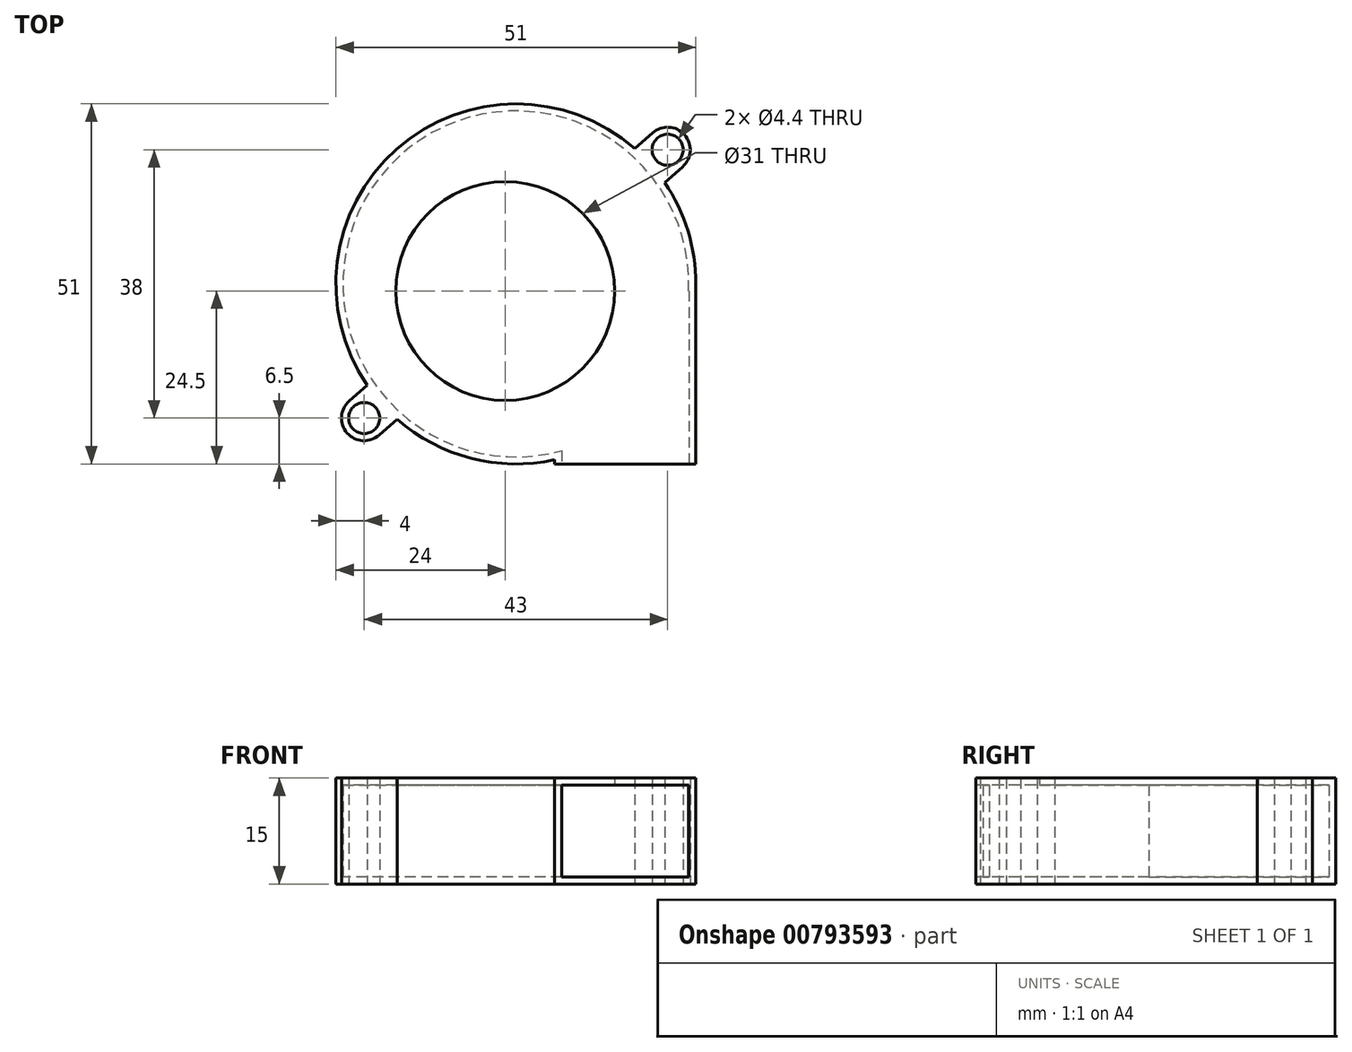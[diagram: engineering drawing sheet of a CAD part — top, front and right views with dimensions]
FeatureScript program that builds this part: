
annotation { "Feature Type Name" : "Feature", "Feature Type Description" : "" }
export const myFeature = defineFeature(function(context is Context, id is Id, definition is map)
    precondition{}
    {
        {
            assignVariable(context, id + "F0", {"name" : "thickness", "anyValue" : 15});
        }
        {
            var Q0;
            Q0=qCreatedBy(makeId("Top.planeOp"),FACE);
            var sketch = newSketch(context, id + "F1", { "sketchPlane" : qUnion([Q0])});
            skLineSegment(sketch, "E0.bottom", {"start": v(25.5, -25.5) * mm, "end": v(-25.5, -25.5) * mm});
            skLineSegment(sketch, "E0.top", {"start": v(25.5, 25.5) * mm, "end": v(-25.5, 25.5) * mm});
            skLineSegment(sketch, "E0.left", {"start": v(25.5, -25.5) * mm, "end": v(25.5, 25.5) * mm});
            skLineSegment(sketch, "E0.right", {"start": v(-25.5, -25.5) * mm, "end": v(-25.5, 25.5) * mm});
            skPoint(sketch, "E0.middle", {"position": v(0, 0) * mm});
            skLineSegment(sketch, "E1.bottom", {"start": v(21.5, -19) * mm, "end": v(-21.5, -19) * mm, "construction": true});
            skLineSegment(sketch, "E1.top", {"start": v(21.5, 19) * mm, "end": v(-21.5, 19) * mm, "construction": true});
            skLineSegment(sketch, "E1.left", {"start": v(21.5, -19) * mm, "end": v(21.5, 19) * mm, "construction": true});
            skLineSegment(sketch, "E1.right", {"start": v(-21.5, -19) * mm, "end": v(-21.5, 19) * mm, "construction": true});
            skCircle(sketch, "E2", {"center": v(0, 0) * mm, "radius": 25.5 * mm});
            skCircle(sketch, "E3", {"center": v(-21.5, -19) * mm, "radius": 2.2 * mm});
            skCircle(sketch, "E4", {"center": v(21.5, 19) * mm, "radius": 2.2 * mm});
            skCircle(sketch, "E5", {"center": v(-21.5, -19) * mm, "radius": 3.2 * mm});
            skCircle(sketch, "E6", {"center": v(21.5, 19) * mm, "radius": 3.2 * mm});
            skLineSegment(sketch, "E7", {"start": v(-21.5, -19) * mm, "end": v(0, 0) * mm, "construction": true});
            skLineSegment(sketch, "E8", {"start": v(21.5, 19) * mm, "end": v(0, 0) * mm, "construction": true});
            skLineSegment(sketch, "E9", {"start": v(-23.62, -16.6) * mm, "end": v(-21.08, -14.35) * mm});
            skLineSegment(sketch, "E10", {"start": v(-19.38, -21.4) * mm, "end": v(-16.84, -19.15) * mm});
            skLineSegment(sketch, "E11", {"start": v(19.38, 21.4) * mm, "end": v(16.84, 19.15) * mm});
            skLineSegment(sketch, "E12", {"start": v(23.62, 16.6) * mm, "end": v(21.08, 14.35) * mm});
            skLineSegment(sketch, "E13", {"start": v(5.5, -25.5) * mm, "end": v(5.5, -24.9) * mm});
            skCircle(sketch, "E14", {"center": v(-1.5, -1) * mm, "radius": 15.5 * mm});
            skCircle(sketch, "E15", {"center": v(0, 0) * mm, "radius": 24.5 * mm});
            skSolve(sketch);
        }
        {
            var Q0;
            {var subQ3=sQuery(id+"F1.wireOp",EDGE,"E13");Q0=makeQuery(id+"F1.imprint","IMPRINT",FACE,{"disambiguationData":[TD([[makeQuery(id+"F1.imprint","IMPRINT",EDGE,{"derivedFrom":subQ3}),-1.0]])]});}
            var Q1;
            Q1=makeQuery(id+"F1.imprint","IMPRINT",FACE,{"disambiguationData":[TD([[makeQuery(id+"F1.imprint","IMPRINT",EDGE,{"derivedFrom":sQuery(id+"F1.wireOp",EDGE,"E14")}),-1.0]])]});
            var Q2;
            {var subQ0=sQuery(id+"F1.wireOp",EDGE,"E10");Q2=makeQuery(id+"F1.imprint","IMPRINT",FACE,{"disambiguationData":[TD([[makeQuery(id+"F1.imprint","IMPRINT",EDGE,{"derivedFrom":subQ0}),1.0]])]});}
            var Q3;
            Q3=makeQuery(id+"F1.imprint","IMPRINT",FACE,{"disambiguationData":[TD([[makeQuery(id+"F1.imprint","IMPRINT",EDGE,{"derivedFrom":sQuery(id+"F1.wireOp",EDGE,"E3")}),-1.0]])]});
            var Q4;
            {var subQ0=sQuery(id+"F1.wireOp",EDGE,"E9");Q4=makeQuery(id+"F1.imprint","IMPRINT",FACE,{"disambiguationData":[TD([[makeQuery(id+"F1.imprint","IMPRINT",EDGE,{"derivedFrom":subQ0}),-1.0]])]});}
            var Q5;
            {var subQ0=sQuery(id+"F1.wireOp",EDGE,"E12");Q5=makeQuery(id+"F1.imprint","IMPRINT",FACE,{"disambiguationData":[TD([[makeQuery(id+"F1.imprint","IMPRINT",EDGE,{"derivedFrom":subQ0}),-1.0]])]});}
            var Q6;
            {var subQ0=sQuery(id+"F1.wireOp",EDGE,"E11");Q6=makeQuery(id+"F1.imprint","IMPRINT",FACE,{"disambiguationData":[TD([[makeQuery(id+"F1.imprint","IMPRINT",EDGE,{"derivedFrom":subQ0}),1.0]])]});}
            var Q7;
            Q7=makeQuery(id+"F1.imprint","IMPRINT",FACE,{"disambiguationData":[TD([[makeQuery(id+"F1.imprint","IMPRINT",EDGE,{"derivedFrom":sQuery(id+"F1.wireOp",EDGE,"E4")}),-1.0]])]});
            var Q8;
            Q8=makeQuery(id+"F1.imprint","IMPRINT",FACE,{"disambiguationData":[TD([[makeQuery(id+"F1.imprint","IMPRINT",EDGE,{"derivedFrom":sQuery(id+"F1.wireOp",EDGE,"E14")}),1.0]])]});
            var Q9;
            Q9=makeQuery(id+"F1.imprint","IMPRINT",FACE,{"disambiguationData":[TD([[makeQuery(id+"F1.imprint","IMPRINT",EDGE,{"derivedFrom":sQuery(id+"F1.wireOp",EDGE,"E15")}),-1.0]])]});
            var Q10;
            {var subQ0=sQuery(id+"F1.wireOp",EDGE,"E5");var subQ1=sQuery(id+"F1.wireOp",EDGE,"E2");var subQ2=makeQuery(id+"F1.imprint","INTERSECT",VERTEX,{"disambiguationData":[OD(0.0)],"derivedFrom":[subQ1,subQ0]});Q10=makeQuery(id+"F1.imprint","IMPRINT",FACE,{"disambiguationData":[TD([[makeQuery(id+"F1.imprint","IMPRINT",EDGE,{"disambiguationData":[TD([[subQ2,-1.0]])],"derivedFrom":subQ1}),1.0]])]});}
            var Q11;
            {var subQ0=sQuery(id+"F1.wireOp",EDGE,"E6");var subQ1=sQuery(id+"F1.wireOp",EDGE,"E2");var subQ2=makeQuery(id+"F1.imprint","INTERSECT",VERTEX,{"disambiguationData":[OD(0.0)],"derivedFrom":[subQ1,subQ0]});Q11=makeQuery(id+"F1.imprint","IMPRINT",FACE,{"disambiguationData":[TD([[makeQuery(id+"F1.imprint","IMPRINT",EDGE,{"disambiguationData":[TD([[subQ2,-1.0]])],"derivedFrom":subQ1}),1.0]])]});}
            extrude(context, id + "F2", {"entities" : qUnion([Q0, Q1, Q2, Q3, Q4, Q5, Q6, Q7, Q8, Q9, Q10, Q11]), "depth" : (getVariable(context, 'thickness')) * mm, "offsetDistance" : 25 * mm});
        }
        {
            var Q0;
            Q0=makeQuery(id+"F1.imprint","IMPRINT",FACE,{"disambiguationData":[TD([[makeQuery(id+"F1.imprint","IMPRINT",EDGE,{"derivedFrom":sQuery(id+"F1.wireOp",EDGE,"E14")}),1.0]])]});
            extrude(context, id + "F3", {"entities" : qUnion([Q0]), "operationType" : NewBodyOperationType.REMOVE, "depth" : 25 * mm, "offsetDistance" : 25 * mm, "hasSecondDirection" : true, "secondDirectionOppositeDirection" : false, "secondDirectionDepth" : 1 * mm});
        }
        {
            var Q0;
            Q0=makeQuery(id+"F1.imprint","IMPRINT",FACE,{"disambiguationData":[TD([[makeQuery(id+"F1.imprint","IMPRINT",EDGE,{"derivedFrom":sQuery(id+"F1.wireOp",EDGE,"E14")}),-1.0]])]});
            var Q1;
            Q1=makeQuery(id+"F1.imprint","IMPRINT",FACE,{"disambiguationData":[TD([[makeQuery(id+"F1.imprint","IMPRINT",EDGE,{"derivedFrom":sQuery(id+"F1.wireOp",EDGE,"E14")}),1.0]])]});
            extrude(context, id + "F4", {"entities" : qUnion([Q0, Q1]), "operationType" : NewBodyOperationType.REMOVE, "depth" : (getVariable(context, 'thickness') - 1) * mm, "offsetDistance" : 25 * mm, "hasSecondDirection" : true, "secondDirectionOppositeDirection" : false, "secondDirectionDepth" : 1 * mm});
        }
        {
            var Q0;
            Q0=makeQuery(id+"F2.opExtrude","SWEPT_FACE",FACE,{"disambiguationData":[OSD([sQuery(id+"F1.wireOp",EDGE,"E0.bottom")])]});
            var sketch = newSketch(context, id + "F5", { "sketchPlane" : qUnion([Q0])});
            skLineSegment(sketch, "E16.bottom", {"start": v(24.5, 1) * mm, "end": v(6.5, 1) * mm});
            skLineSegment(sketch, "E16.top", {"start": v(24.5, 14) * mm, "end": v(6.5, 14) * mm});
            skLineSegment(sketch, "E16.left", {"start": v(24.5, 1) * mm, "end": v(24.5, 14) * mm});
            skLineSegment(sketch, "E16.right", {"start": v(6.5, 1) * mm, "end": v(6.5, 14) * mm});
            skPoint(sketch, "E16.middle", {"position": v(15.5, 7.5) * mm});
            skPoint(sketch, "E16.middle.positionSnap0", {"position": v(5.5, 7.5) * mm});
            skPoint(sketch, "E16.middle.positionSnap1", {"position": v(15.5, 15) * mm});
            skPoint(sketch, "E16.centerSnap0", {"position": v(5.5, 7.5) * mm});
            skPoint(sketch, "E16.centerSnap1", {"position": v(15.5, 15) * mm});
            skSolve(sketch);
        }
        {
            var Q0;
            Q0=makeQuery(id+"F5.imprint","IMPRINT",FACE,{"disambiguationData":[TD([[makeQuery(id+"F5.imprint","IMPRINT",EDGE,{"derivedFrom":sQuery(id+"F5.wireOp",EDGE,"E16.bottom")}),-1.0]])]});
            var Q1;
            Q1=sQuery(id+"F1.wireOp",VERTEX,"E14.center");
            extrude(context, id + "F6", {"entities" : qUnion([Q0]), "operationType" : NewBodyOperationType.REMOVE, "endBound" : BoundingType.UP_TO_VERTEX, "oppositeDirection" : true, "depth" : 25 * mm, "endBoundEntityVertex" : qUnion([Q1]), "offsetDistance" : 25 * mm});
        }
    });
